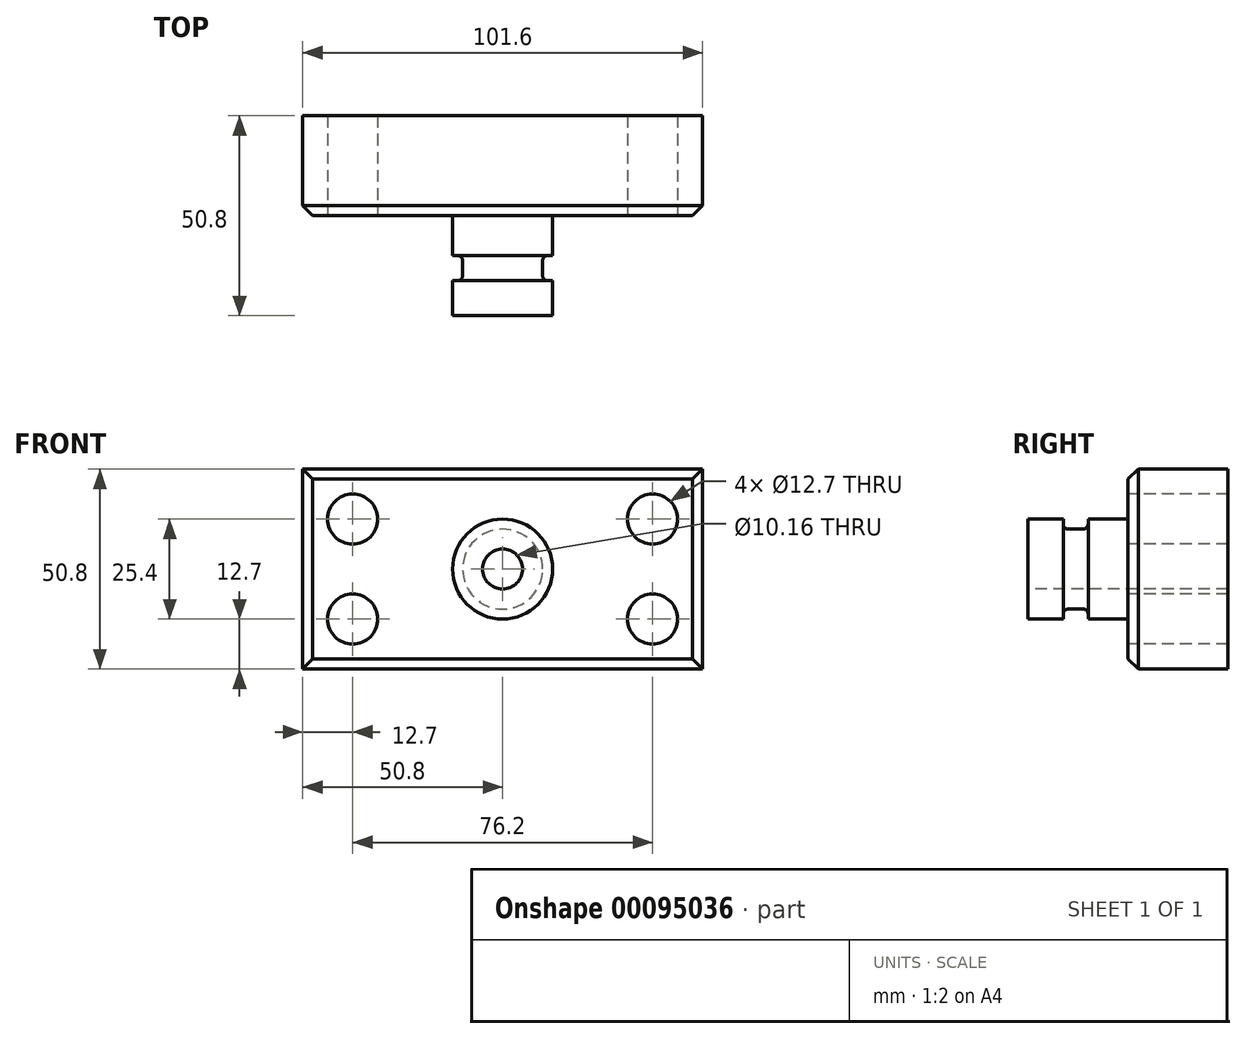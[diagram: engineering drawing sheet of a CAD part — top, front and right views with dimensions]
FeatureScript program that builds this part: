
annotation { "Feature Type Name" : "Feature", "Feature Type Description" : "" }
export const myFeature = defineFeature(function(context is Context, id is Id, definition is map)
    precondition{}
    {
        {
            var Q0;
            Q0=qCreatedBy(makeId("Front.planeOp"),FACE);
            var sketch = newSketch(context, id + "F0", { "sketchPlane" : qUnion([Q0])});
            skLineSegment(sketch, "E0.bottom", {"start": v(50.8, 25.4) * mm, "end": v(-50.8, 25.4) * mm});
            skLineSegment(sketch, "E0.top", {"start": v(50.8, -25.4) * mm, "end": v(-50.8, -25.4) * mm});
            skLineSegment(sketch, "E0.left", {"start": v(50.8, 25.4) * mm, "end": v(50.8, -25.4) * mm});
            skLineSegment(sketch, "E0.right", {"start": v(-50.8, 25.4) * mm, "end": v(-50.8, -25.4) * mm});
            skPoint(sketch, "E0.middle", {"position": v(0, 0) * mm});
            skSolve(sketch);
        }
        {
            var Q0;
            Q0=makeQuery(id+"F0.imprint","IMPRINT",FACE,{"disambiguationData":[TD([[makeQuery(id+"F0.imprint","IMPRINT",EDGE,{"derivedFrom":sQuery(id+"F0.wireOp",EDGE,"E0.bottom")}),1.0]])]});
            extrude(context, id + "F1", {"entities" : qUnion([Q0]), "depth" : 25.4 * mm});
        }
        {
            var Q0;
            Q0=makeQuery(id+"F1.opExtrude","CAP_FACE",FACE,{"disambiguationData":[OSD([sQuery(id+"F0.wireOp",EDGE,"E0.bottom"),sQuery(id+"F0.wireOp",EDGE,"E0.top"),sQuery(id+"F0.wireOp",EDGE,"E0.left"),sQuery(id+"F0.wireOp",EDGE,"E0.right")])],"isStart":false});
            var sketch = newSketch(context, id + "F2", { "sketchPlane" : qUnion([Q0])});
            skPoint(sketch, "E1.middle", {"position": v(0, 0) * mm});
            skCircle(sketch, "E2", {"center": v(-38.1, 12.7) * mm, "radius": 6.35 * mm});
            skCircle(sketch, "E3", {"center": v(-38.1, -12.7) * mm, "radius": 6.35 * mm});
            skCircle(sketch, "E4", {"center": v(38.1, -12.7) * mm, "radius": 6.35 * mm});
            skCircle(sketch, "E5", {"center": v(38.1, 12.7) * mm, "radius": 6.35 * mm});
            skSolve(sketch);
        }
        {
            var Q0;
            Q0=makeQuery(id+"F2.imprint","IMPRINT",FACE,{"disambiguationData":[TD([[makeQuery(id+"F2.imprint","IMPRINT",EDGE,{"derivedFrom":sQuery(id+"F2.wireOp",EDGE,"E2")}),1.0]])]});
            var Q1;
            Q1=makeQuery(id+"F2.imprint","IMPRINT",FACE,{"disambiguationData":[TD([[makeQuery(id+"F2.imprint","IMPRINT",EDGE,{"derivedFrom":sQuery(id+"F2.wireOp",EDGE,"E5")}),1.0]])]});
            var Q2;
            Q2=makeQuery(id+"F2.imprint","IMPRINT",FACE,{"disambiguationData":[TD([[makeQuery(id+"F2.imprint","IMPRINT",EDGE,{"derivedFrom":sQuery(id+"F2.wireOp",EDGE,"E4")}),1.0]])]});
            var Q3;
            Q3=makeQuery(id+"F2.imprint","IMPRINT",FACE,{"disambiguationData":[TD([[makeQuery(id+"F2.imprint","IMPRINT",EDGE,{"derivedFrom":sQuery(id+"F2.wireOp",EDGE,"E3")}),1.0]])]});
            extrude(context, id + "F3", {"entities" : qUnion([Q0, Q1, Q2, Q3]), "operationType" : NewBodyOperationType.REMOVE, "endBound" : BoundingType.THROUGH_ALL, "oppositeDirection" : true, "depth" : 25.4 * mm});
        }
        {
            var Q0;
            Q0=qCreatedBy(makeId("Top.planeOp"),FACE);
            var sketch = newSketch(context, id + "F4", { "sketchPlane" : qUnion([Q0])});
            skLineSegment(sketch, "E6.bottom", {"start": v(0, -25.4) * mm, "end": v(12.7, -25.4) * mm});
            skLineSegment(sketch, "E6.top", {"start": v(0, -50.8) * mm, "end": v(12.7, -50.8) * mm});
            skLineSegment(sketch, "E6.left", {"start": v(0, -25.4) * mm, "end": v(0, -50.8) * mm});
            skLineSegment(sketch, "E6.right", {"start": v(12.7, -25.4) * mm, "end": v(12.7, -50.8) * mm});
            skSolve(sketch);
        }
        {
            var Q0;
            Q0 = qSketchRegion(id + "F4", true);
            var Q1;
            Q1=sQuery(id+"F4.wireOp",EDGE,"E6.left");
            revolve(context, id + "F5", {"operationType" : NewBodyOperationType.ADD, "entities" : qUnion([Q0]), "axis" : qUnion([Q1]), "revolveType" : RevolveType.FULL});
        }
        {
            var Q0;
            Q0=qCreatedBy(makeId("Top.planeOp"),FACE);
            var sketch = newSketch(context, id + "F6", { "sketchPlane" : qUnion([Q0])});
            skLineSegment(sketch, "E7.bottom", {"start": v(-25.05, -41.91) * mm, "end": v(-10.16, -41.91) * mm});
            skLineSegment(sketch, "E7.top", {"start": v(-25.05, -35.56) * mm, "end": v(-10.16, -35.56) * mm});
            skLineSegment(sketch, "E7.left", {"start": v(-25.05, -41.91) * mm, "end": v(-25.05, -35.56) * mm});
            skLineSegment(sketch, "E7.right", {"start": v(-10.16, -41.91) * mm, "end": v(-10.16, -35.56) * mm});
            skLineSegment(sketch, "E8", {"start": v(0, -70.11) * mm, "end": v(0, 0) * mm, "construction": true});
            skSolve(sketch);
        }
        {
            var Q0;
            Q0 = qSketchRegion(id + "F6", true);
            var Q1;
            Q1=sQuery(id+"F6.wireOp",EDGE,"E8");
            revolve(context, id + "F7", {"operationType" : NewBodyOperationType.REMOVE, "entities" : qUnion([Q0]), "axis" : qUnion([Q1]), "revolveType" : RevolveType.FULL, "oppositeDirection" : true});
        }
        {
            var Q0;
            Q0=makeQuery(id+"F5.opRevolve","SWEPT_EDGE",EDGE,{"disambiguationData":[OSD([sQuery(id+"F4.wireOp",EDGE,"E6.bottom"),sQuery(id+"F4.wireOp",EDGE,"E6.right")])]});
            var Q1;
            Q1=makeQuery(id+"F7.boolean.opBoolean","COPY",EDGE,{"derivedFrom":makeQuery(id+"F7.opRevolve","SWEPT_EDGE",EDGE,{"disambiguationData":[OSD([sQuery(id+"F6.wireOp",EDGE,"E7.top"),sQuery(id+"F6.wireOp",EDGE,"E7.right")])]})});
            var Q2;
            Q2=makeQuery(id+"F7.boolean.opBoolean","COPY",EDGE,{"derivedFrom":makeQuery(id+"F7.opRevolve","SWEPT_EDGE",EDGE,{"disambiguationData":[OSD([sQuery(id+"F6.wireOp",EDGE,"E7.bottom"),sQuery(id+"F6.wireOp",EDGE,"E7.right")])]})});
            fillet(context, id + "F8", {"entities" : qUnion([Q0, Q1, Q2]), "radius" : 1.27 * mm, "tangentPropagation" : true, "allowEdgeOverflow" : false});
        }
        {
            var Q0;
            Q0=makeQuery(id+"F1.opExtrude","CAP_EDGE",EDGE,{"disambiguationData":[OSD([sQuery(id+"F0.wireOp",EDGE,"E0.top")])],"isStart":false});
            var Q1;
            Q1=makeQuery(id+"F1.opExtrude","CAP_EDGE",EDGE,{"disambiguationData":[OSD([sQuery(id+"F0.wireOp",EDGE,"E0.bottom")])],"isStart":false});
            var Q2;
            Q2=makeQuery(id+"F1.opExtrude","CAP_EDGE",EDGE,{"disambiguationData":[OSD([sQuery(id+"F0.wireOp",EDGE,"E0.left")])],"isStart":false});
            var Q3;
            Q3=makeQuery(id+"F1.opExtrude","CAP_EDGE",EDGE,{"disambiguationData":[OSD([sQuery(id+"F0.wireOp",EDGE,"E0.right")])],"isStart":false});
            chamfer(context, id + "F9", {"entities" : qUnion([Q0, Q1, Q2, Q3]), "width" : 2.54 * mm, "tangentPropagation" : true});
        }
        {
            var Q0;
            Q0=makeQuery(id+"F5.opRevolve","SWEPT_FACE",FACE,{"disambiguationData":[OSD([sQuery(id+"F4.wireOp",EDGE,"E6.top")])]});
            var sketch = newSketch(context, id + "F10", { "sketchPlane" : qUnion([Q0])});
            skCircle(sketch, "E9", {"center": v(0, 0) * mm, "radius": 5.08 * mm});
            skSolve(sketch);
        }
        {
            var Q0;
            Q0=makeQuery(id+"F10.imprint","IMPRINT",FACE,{"disambiguationData":[TD([[makeQuery(id+"F10.imprint","IMPRINT",EDGE,{"derivedFrom":sQuery(id+"F10.wireOp",EDGE,"E9")}),1.0]])]});
            extrude(context, id + "F11", {"entities" : qUnion([Q0]), "operationType" : NewBodyOperationType.REMOVE, "endBound" : BoundingType.THROUGH_ALL, "oppositeDirection" : true, "depth" : 25.4 * mm});
        }
    });
